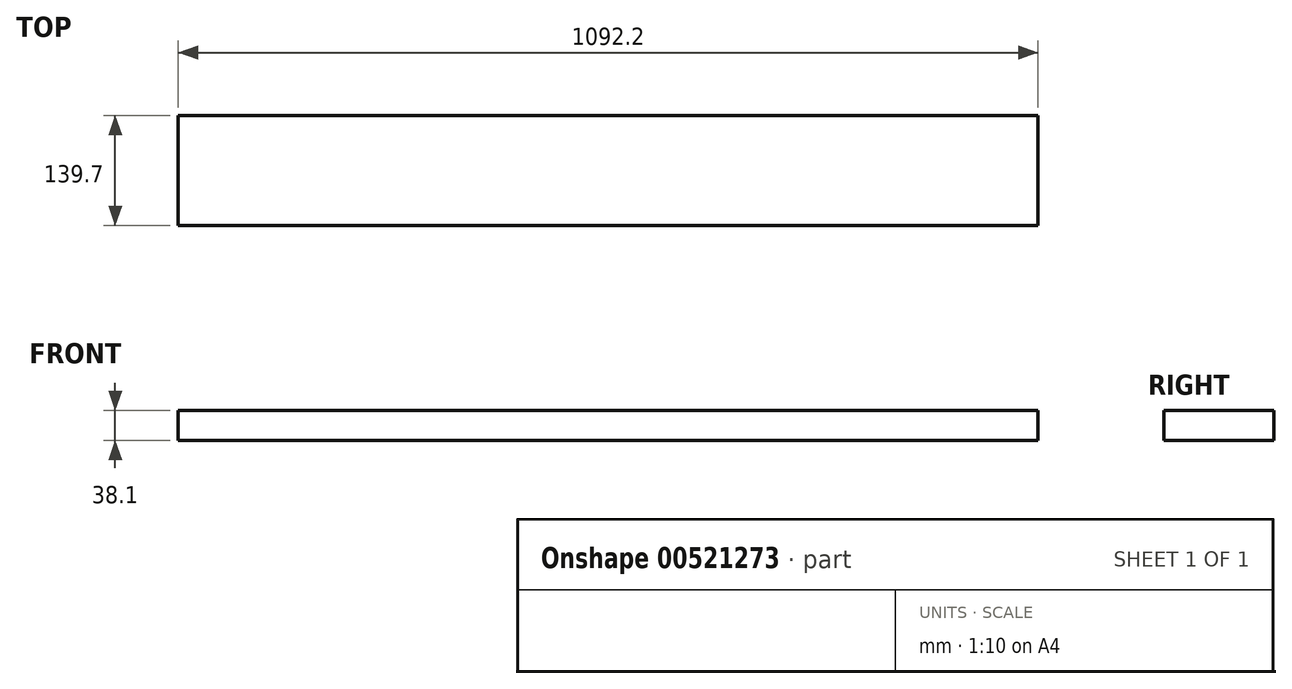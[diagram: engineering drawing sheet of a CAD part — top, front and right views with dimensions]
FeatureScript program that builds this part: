
annotation { "Feature Type Name" : "Feature", "Feature Type Description" : "" }
export const myFeature = defineFeature(function(context is Context, id is Id, definition is map)
    precondition{}
    {
        {
            var Q0;
            Q0=qCreatedBy(makeId("Front.planeOp"),FACE);
            var sketch = newSketch(context, id + "F0", { "sketchPlane" : qUnion([Q0])});
            skLineSegment(sketch, "E0", {"start": v(546.1, 0) * mm, "end": v(-546.1, 0) * mm});
            skLineSegment(sketch, "E1", {"start": v(0, 570.25) * mm, "end": v(0, -656.25) * mm});
            skLineSegment(sketch, "E2", {"start": v(-546.1, 0) * mm, "end": v(-546.1, 38.1) * mm});
            skLineSegment(sketch, "E3", {"start": v(-546.1, 38.1) * mm, "end": v(546.1, 38.1) * mm});
            skLineSegment(sketch, "E4", {"start": v(546.1, 38.1) * mm, "end": v(546.1, 0) * mm});
            skSolve(sketch);
        }
        {
            var Q0;
            {var subQ0=sQuery(id+"F0.wireOp",EDGE,"E4");Q0=makeQuery(id+"F0.imprint","IMPRINT",FACE,{"disambiguationData":[TD([[makeQuery(id+"F0.imprint","IMPRINT",EDGE,{"derivedFrom":subQ0}),-1.0]])]});}
            var Q1;
            {var subQ0=sQuery(id+"F0.wireOp",EDGE,"E2");Q1=makeQuery(id+"F0.imprint","IMPRINT",FACE,{"disambiguationData":[TD([[makeQuery(id+"F0.imprint","IMPRINT",EDGE,{"derivedFrom":subQ0}),-1.0]])]});}
            extrude(context, id + "F1", {"entities" : qUnion([Q0, Q1]), "depth" : 139.7 * mm, "offsetDistance" : 25.4 * mm});
        }
    });
